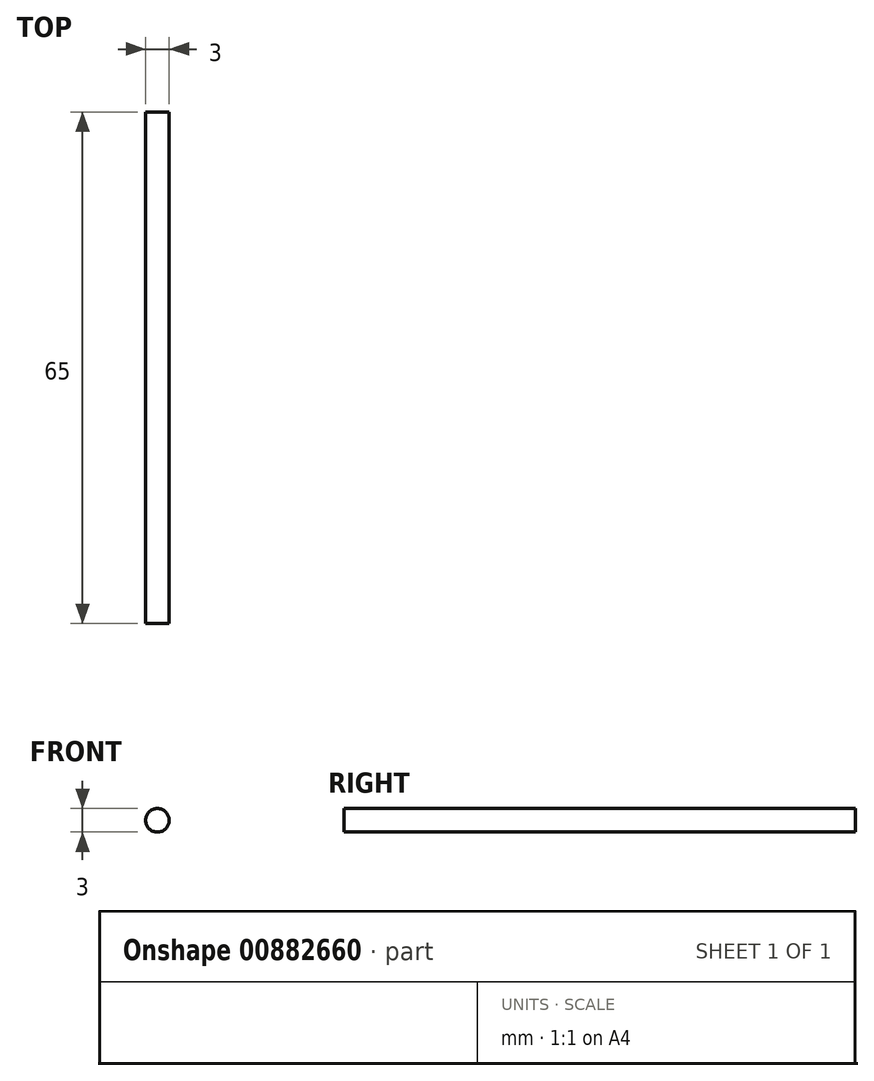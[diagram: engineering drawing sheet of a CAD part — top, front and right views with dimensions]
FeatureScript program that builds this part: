
annotation { "Feature Type Name" : "Feature", "Feature Type Description" : "" }
export const myFeature = defineFeature(function(context is Context, id is Id, definition is map)
    precondition{}
    {
        {
            var Q0;
            Q0=qCreatedBy(makeId("Front.planeOp"),FACE);
            var sketch = newSketch(context, id + "F0", { "sketchPlane" : qUnion([Q0])});
            skCircle(sketch, "E0", {"center": v(0, 0) * mm, "radius": 1.5 * mm});
            skSolve(sketch);
        }
        {
            var Q0;
            Q0 = qSketchRegion(id + "F0", true);
            extrude(context, id + "F1", {"entities" : qUnion([Q0]), "depth" : 65 * mm, "offsetDistance" : 25 * mm});
        }
    });
